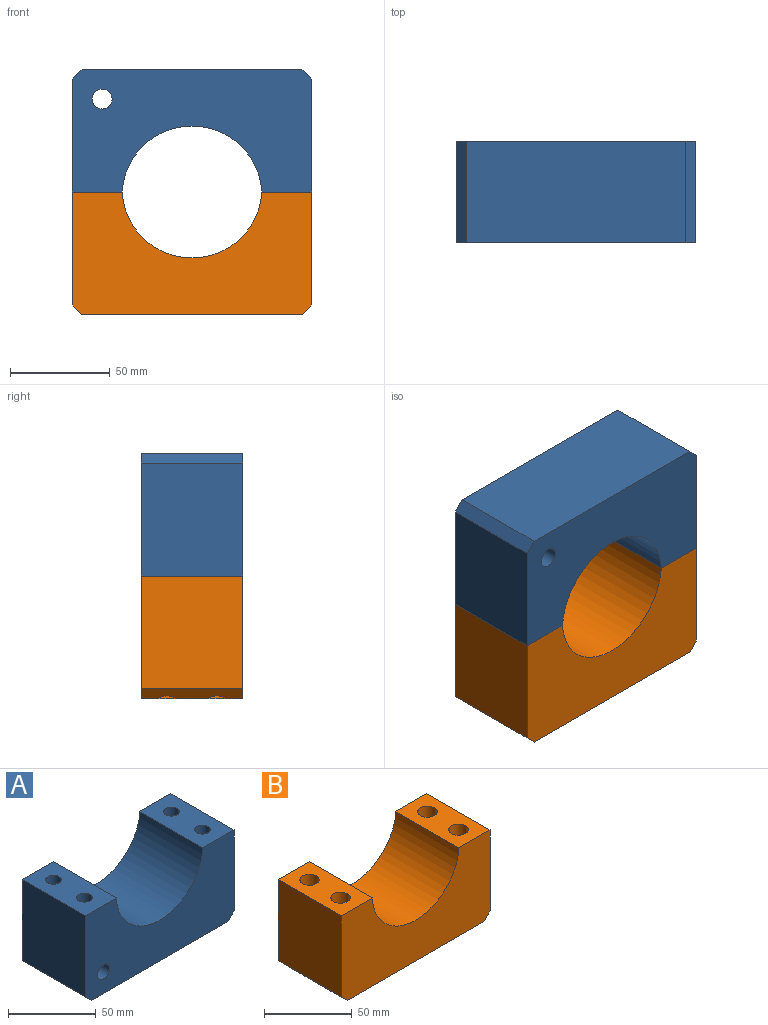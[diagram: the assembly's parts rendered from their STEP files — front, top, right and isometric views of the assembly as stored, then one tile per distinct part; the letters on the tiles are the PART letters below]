
ASSEMBLY  parts=2 mates=1
PART A: 21 faces, bbox 120x50.8x61.5 mm
  f0: plane 56.5x50.8mm, normal (-1,0,0), area 2870.2mm2, adj f4,f5,f6,f16
  f1: plane 110x50.8mm, normal (0,0,-1), area 5588mm2, adj f4,f5,f16,f17
  f2: plane 56.5x50.8mm, normal (1,0,0), area 2809.4mm2, adj f4,f5,f9,f17,f20
  f3: cylinder r=35mm len=69.89mm, axis (0,1,0), area 5382.4mm2, adj f4,f5,f6,f9
  f4: plane 120x61.5mm, normal (0,-1,0), area 5492.2mm2, adj f0,f1,f2,f3,f6,f9,f16,f17
  f5: plane 120x61.5mm, normal (0,1,0), area 5492.2mm2, adj f0,f1,f2,f3,f6,f9,f16,f17
  f6: plane 50.8x25.06mm, normal (0,0,1), area 1151.3mm2, adj f0,f3,f4,f5,f8,f13
  f7: cone r=4.4mm half-angle=59deg, axis (0,0,1), area 71mm2, adj f8
  f8: cylinder r=4.4mm len=29.25mm, axis (0,0,1), area 808.6mm2, adj f6,f7
  f9: plane 50.8x25.06mm, normal (0,0,1), area 1151.3mm2, adj f2,f3,f4,f5,f11,f15
  f10: cone r=4.4mm half-angle=59deg, axis (0,0,1), area 71mm2, adj f11
  f11: cylinder r=4.4mm len=29.25mm, axis (0,0,1), area 808.6mm2, adj f9,f10
  f12: cone r=4.4mm half-angle=59deg, axis (0,0,1), area 71mm2, adj f13
  f13: cylinder r=4.4mm len=29.25mm, axis (0,0,1), area 808.6mm2, adj f6,f12
  f14: cone r=4.4mm half-angle=59deg, axis (0,0,1), area 71mm2, adj f15
  f15: cylinder r=4.4mm len=29.25mm, axis (0,0,1), area 808.6mm2, adj f9,f14
  f16: plane 50.8x5mm, normal (-0.71,0,-0.71), area 359.2mm2, adj f0,f1,f4,f5
  f17: plane 50.8x5mm, normal (0.71,0,-0.71), area 359.2mm2, adj f1,f2,f4,f5
  f18: cylinder r=5mm len=50.8mm, axis (0,1,0), area 1595.9mm2, adj f4,f5
  f19: cone r=4.4mm half-angle=59deg, axis (1,0,0), area 71mm2, adj f20
  f20: cylinder r=4.4mm len=26.25mm, axis (1,0,0), area 725.7mm2, adj f2,f19
PART B: 22 faces, bbox 120x50.8x61.5 mm
  f0: plane 56.5x50.8mm, normal (-1,0,0), area 2870.2mm2, adj f4,f5,f7,f8
  f1: plane 110x50.8mm, normal (0,0,-1), area 4610.6mm2, adj f4,f5,f8,f9,f12,f15,f18,f21
  f2: plane 56.5x50.8mm, normal (1,0,0), area 2870.2mm2, adj f4,f5,f6,f9
  f3: cylinder r=35mm len=69.89mm, axis (0,1,0), area 5382.4mm2, adj f4,f5,f6,f7
  f4: plane 120x61.5mm, normal (0,-1,0), area 5570.7mm2, adj f0,f1,f2,f3,f6,f7,f8,f9
  f5: plane 120x61.5mm, normal (0,1,0), area 5570.7mm2, adj f0,f1,f2,f3,f6,f7,f8,f9
  f6: plane 50.8x25.06mm, normal (0,0,1), area 1082.8mm2, adj f2,f3,f4,f5,f10,f13
  f7: plane 50.8x25.06mm, normal (0,0,1), area 1082.8mm2, adj f0,f3,f4,f5,f16,f19
  f8: plane 50.8x5mm, normal (-0.71,0,-0.71), area 330.6mm2, adj f0,f1,f4,f5,f18,f21
  f9: plane 50.8x5mm, normal (0.71,0,-0.71), area 330.6mm2, adj f1,f2,f4,f5,f12,f15
  f10: cylinder r=5.5mm len=31.5mm, axis (0,0,-1), area 1088.6mm2, adj f6,f11
  f11: plane 18x18mm, normal (0,0,-1), area 159.4mm2, adj f10,f12
  f12: cylinder r=9mm len=30mm, axis (0,0,-1), area 1686mm2, adj f1,f9,f11
  f13: cylinder r=5.5mm len=31.5mm, axis (0,0,-1), area 1088.6mm2, adj f6,f14
  f14: plane 18x18mm, normal (0,0,-1), area 159.4mm2, adj f13,f15
  f15: cylinder r=9mm len=30mm, axis (0,0,-1), area 1686mm2, adj f1,f9,f14
  f16: cylinder r=5.5mm len=31.5mm, axis (0,0,-1), area 1088.6mm2, adj f7,f17
  f17: plane 18x18mm, normal (0,0,-1), area 159.4mm2, adj f16,f18
  f18: cylinder r=9mm len=30mm, axis (0,0,-1), area 1686mm2, adj f1,f8,f17
  f19: cylinder r=5.5mm len=31.5mm, axis (0,0,-1), area 1088.6mm2, adj f7,f20
  f20: plane 18x18mm, normal (0,0,-1), area 159.4mm2, adj f19,f21
  f21: cylinder r=9mm len=30mm, axis (0,0,-1), area 1686mm2, adj f1,f8,f20
PLACE A rot(axis=(1,0,0),180deg) t=(7.22,3.01,57.72)mm
PLACE B t=(7.22,3.01,-1.78)mm fixed
MATE fastened B.f7 <-> A.f6  axis (0,0,-1) through (-52.78,-22.39,27.97)mm
